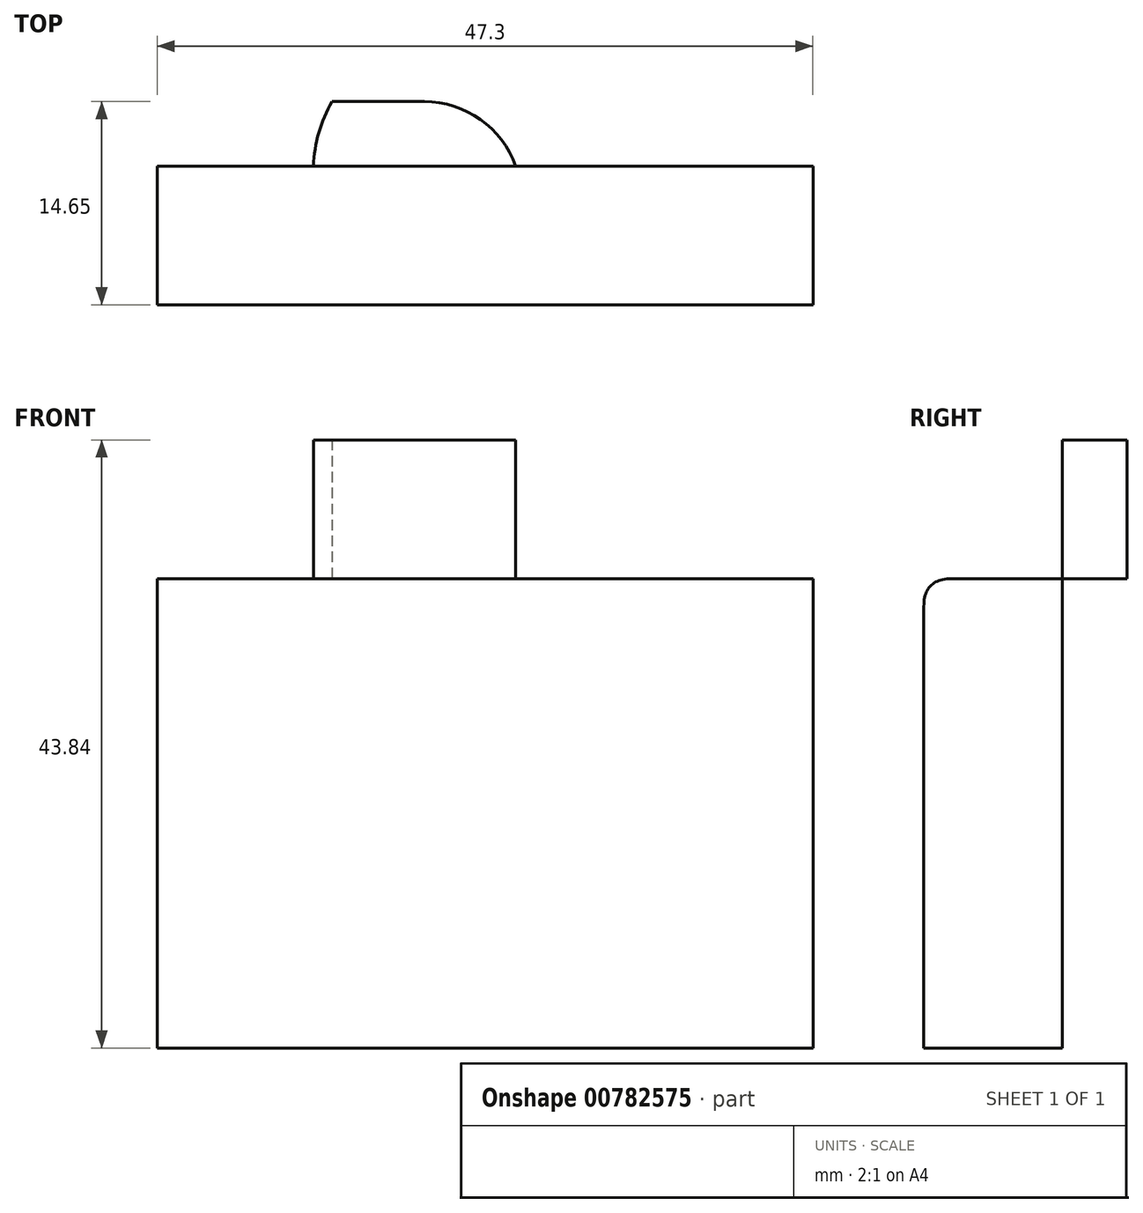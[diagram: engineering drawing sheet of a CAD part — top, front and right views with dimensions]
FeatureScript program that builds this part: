
annotation { "Feature Type Name" : "Feature", "Feature Type Description" : "" }
export const myFeature = defineFeature(function(context is Context, id is Id, definition is map)
    precondition{}
    {
        {
            var Q0;
            Q0=qCreatedBy(makeId("Front.planeOp"),FACE);
            var sketch = newSketch(context, id + "F0", { "sketchPlane" : qUnion([Q0])});
            skLineSegment(sketch, "E0.bottom", {"start": v(0, 0) * mm, "end": v(47.3, 0) * mm});
            skLineSegment(sketch, "E0.top", {"start": v(0, -33.84) * mm, "end": v(47.3, -33.84) * mm});
            skLineSegment(sketch, "E0.left", {"start": v(0, 0) * mm, "end": v(0, -33.84) * mm});
            skLineSegment(sketch, "E0.right", {"start": v(47.3, 0) * mm, "end": v(47.3, -33.84) * mm});
            skSolve(sketch);
        }
        {
            var Q0;
            Q0=makeQuery(id+"F0.imprint","IMPRINT",FACE,{"disambiguationData":[TD([[makeQuery(id+"F0.imprint","IMPRINT",EDGE,{"derivedFrom":sQuery(id+"F0.wireOp",EDGE,"E0.bottom")}),-1.0]])]});
            extrude(context, id + "F1", {"entities" : qUnion([Q0]), "depth" : 10 * mm, "offsetDistance" : 25.4 * mm});
        }
        {
            var Q0;
            Q0=makeQuery(id+"F1.opExtrude","SWEPT_FACE",FACE,{"disambiguationData":[OSD([sQuery(id+"F0.wireOp",EDGE,"E0.bottom")])]});
            var sketch = newSketch(context, id + "F2", { "sketchPlane" : qUnion([Q0])});
            skArc(sketch, "E1", {"start": v(31.27, 0) * mm, "mid": v(21.27, 9.65) * mm, "end": v(11.28, -0.02) * mm});
            skLineSegment(sketch, "E2", {"start": v(11.28, -0.02) * mm, "end": v(31.27, 0) * mm});
            skLineSegment(sketch, "E3", {"start": v(21.28, 0) * mm, "end": v(21.27, 9.65) * mm, "construction": true});
            skLineSegment(sketch, "E4.bottom", {"start": v(19.28, -0.35) * mm, "end": v(5.26, -0.35) * mm});
            skLineSegment(sketch, "E4.top", {"start": v(19.28, -8.08) * mm, "end": v(5.26, -8.08) * mm});
            skLineSegment(sketch, "E4.left", {"start": v(21.28, -2.35) * mm, "end": v(21.28, -6.08) * mm});
            skLineSegment(sketch, "E4.right", {"start": v(3.26, -2.35) * mm, "end": v(3.26, -6.08) * mm});
            skPoint(sketch, "E5.visualSharp", {"position": v(21.28, -8.08) * mm});
            skArc(sketch, "E5.filletArc", {"start": v(19.28, -8.08) * mm, "mid": v(20.7, -7.5) * mm, "end": v(21.28, -6.08) * mm});
            skPoint(sketch, "E6.visualSharp", {"position": v(3.26, -8.08) * mm});
            skArc(sketch, "E6.filletArc", {"start": v(3.26, -6.08) * mm, "mid": v(3.85, -7.5) * mm, "end": v(5.26, -8.08) * mm});
            skPoint(sketch, "E7.visualSharp", {"position": v(3.26, -0.35) * mm});
            skArc(sketch, "E7.filletArc", {"start": v(5.26, -0.35) * mm, "mid": v(3.85, -0.94) * mm, "end": v(3.26, -2.35) * mm});
            skArc(sketch, "E8.filletArc", {"start": v(21.28, -2.35) * mm, "mid": v(20.7, -0.94) * mm, "end": v(19.28, -0.35) * mm});
            skLineSegment(sketch, "E9.0", {"start": v(19.28, 4.65) * mm, "end": v(5.26, 4.65) * mm});
            skArc(sketch, "E10.0", {"start": v(5.26, 4.65) * mm, "mid": v(0.31, 2.6) * mm, "end": v(-1.74, -2.35) * mm});
            skLineSegment(sketch, "E11.0", {"start": v(-1.74, -2.35) * mm, "end": v(-1.74, -6.08) * mm});
            skArc(sketch, "E12.0", {"start": v(-1.74, -6.08) * mm, "mid": v(0.31, -11.03) * mm, "end": v(5.26, -13.08) * mm});
            skLineSegment(sketch, "E13.0", {"start": v(19.28, -13.08) * mm, "end": v(5.26, -13.08) * mm});
            skArc(sketch, "E14.0", {"start": v(19.28, -13.08) * mm, "mid": v(24.23, -11.03) * mm, "end": v(26.28, -6.08) * mm});
            skLineSegment(sketch, "E15.0", {"start": v(26.28, -2.35) * mm, "end": v(26.28, -6.08) * mm});
            skArc(sketch, "E16.0", {"start": v(26.28, -2.35) * mm, "mid": v(24.23, 2.6) * mm, "end": v(19.28, 4.65) * mm});
            skLineSegment(sketch, "E17.0", {"start": v(19.28, -1.35) * mm, "end": v(5.26, -1.35) * mm});
            skSolve(sketch);
        }
        {
            var Q0;
            {var subQ0=sQuery(id+"F2.wireOp",EDGE,"E1");var subQ1=makeQuery(id+"F1.opExtrude","CAP_EDGE",EDGE,{"disambiguationData":[OSD([sQuery(id+"F0.wireOp",EDGE,"E0.bottom")])],"isStart":true});var subQ3=makeQuery(id+"F2.imprint","INTERSECT",VERTEX,{"derivedFrom":[subQ1,subQ0]});Q0=makeQuery(id+"F2.imprint","IMPRINT",FACE,{"disambiguationData":[TD([[makeQuery(id+"F2.imprint","IMPRINT",EDGE,{"disambiguationData":[TD([[subQ3,1.0]])],"derivedFrom":subQ0}),1.0]])]});}
            extrude(context, id + "F3", {"entities" : qUnion([Q0]), "depth" : 10 * mm, "offsetDistance" : 25.4 * mm});
        }
        {
            var Q0;
            Q0=makeQuery(id+"F1.opExtrude","CAP_EDGE",EDGE,{"disambiguationData":[OSD([sQuery(id+"F0.wireOp",EDGE,"E0.bottom")])],"isStart":false});
            fillet(context, id + "F4", {"entities" : qUnion([Q0]), "radius" : 2 * mm, "tangentPropagation" : true, "rho" : 0.5, "crossSection" : FilletCrossSection.CONIC, "allowEdgeOverflow" : false});
        }
    });
